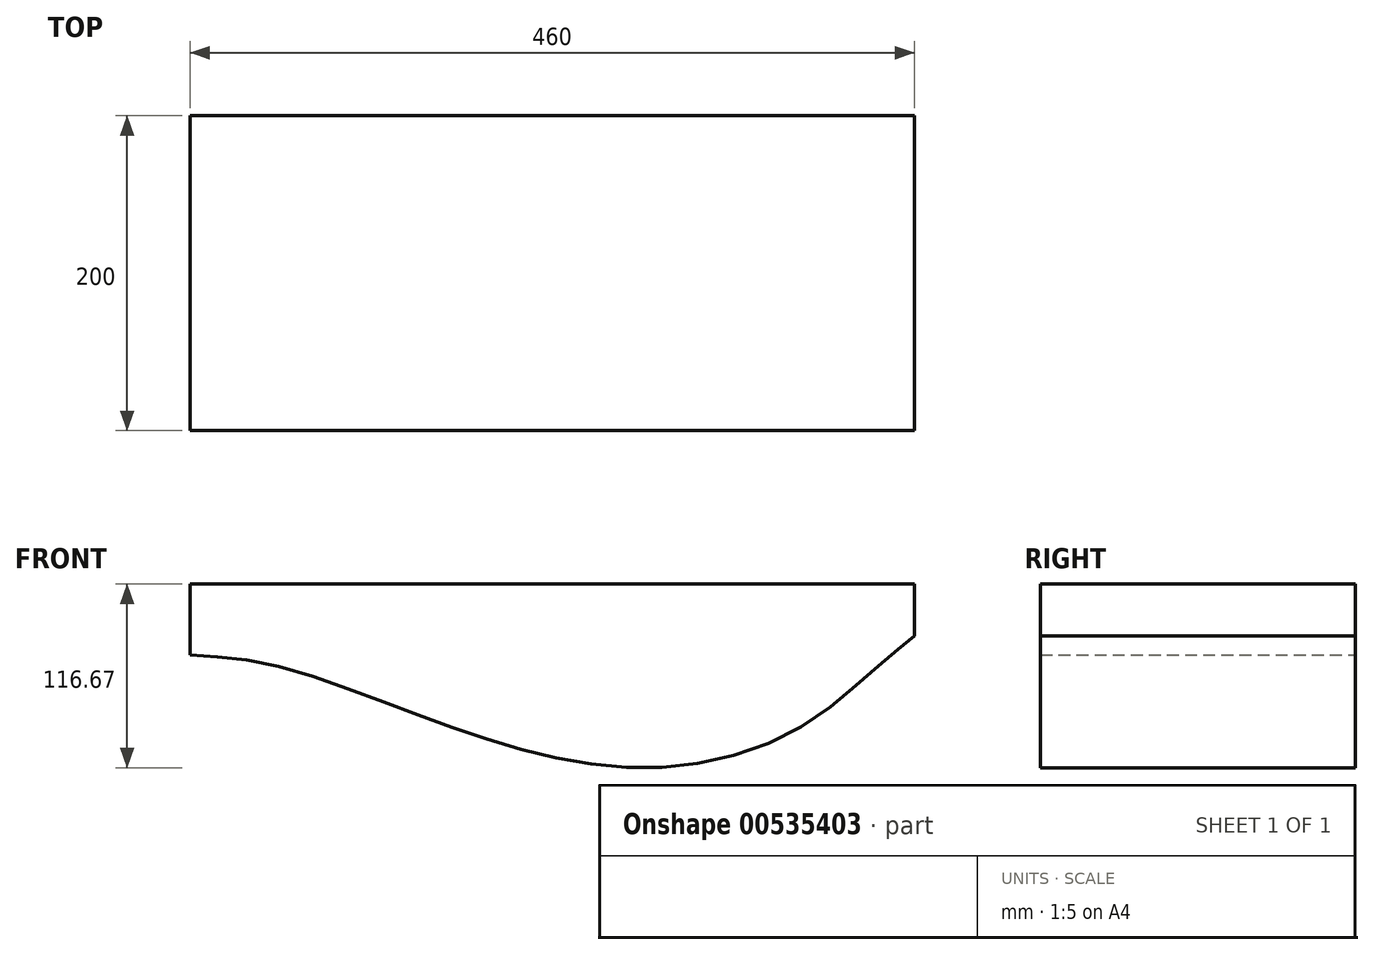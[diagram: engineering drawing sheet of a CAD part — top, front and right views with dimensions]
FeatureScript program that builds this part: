
annotation { "Feature Type Name" : "Feature", "Feature Type Description" : "" }
export const myFeature = defineFeature(function(context is Context, id is Id, definition is map)
    precondition{}
    {
        {
            var Q0;
            Q0=qCreatedBy(makeId("Front.planeOp"),FACE);
            var sketch = newSketch(context, id + "F0", { "sketchPlane" : qUnion([Q0])});
            skLineSegment(sketch, "E0", {"start": v(-101.41, 43.82) * mm, "end": v(358.59, 43.82) * mm});
            skLineSegment(sketch, "E1", {"start": v(-101.41, 43.82) * mm, "end": v(-101.41, -1.18) * mm});
            skLineSegment(sketch, "E2", {"start": v(-78.41, 43.82) * mm, "end": v(-78.41, -3.18) * mm, "construction": true});
            skLineSegment(sketch, "E3", {"start": v(-55.41, 43.82) * mm, "end": v(-55.41, -6.18) * mm, "construction": true});
            skLineSegment(sketch, "E4", {"start": v(-32.41, 43.82) * mm, "end": v(-32.41, -11.18) * mm, "construction": true});
            skLineSegment(sketch, "E5", {"start": v(-9.41, 43.82) * mm, "end": v(-9.41, -19.18) * mm, "construction": true});
            skLineSegment(sketch, "E6", {"start": v(13.59, 43.82) * mm, "end": v(13.59, -28.18) * mm, "construction": true});
            skLineSegment(sketch, "E7", {"start": v(36.59, 43.82) * mm, "end": v(36.59, -36.18) * mm, "construction": true});
            skLineSegment(sketch, "E8", {"start": v(59.59, 43.82) * mm, "end": v(59.59, -45.18) * mm, "construction": true});
            skLineSegment(sketch, "E9", {"start": v(82.59, 43.82) * mm, "end": v(82.59, -53.18) * mm, "construction": true});
            skLineSegment(sketch, "E10", {"start": v(105.59, 43.82) * mm, "end": v(105.59, -60.18) * mm, "construction": true});
            skLineSegment(sketch, "E11", {"start": v(128.59, 43.82) * mm, "end": v(128.59, -66.18) * mm, "construction": true});
            skLineSegment(sketch, "E12", {"start": v(151.59, 43.82) * mm, "end": v(151.59, -70.18) * mm, "construction": true});
            skLineSegment(sketch, "E13", {"start": v(174.59, 43.82) * mm, "end": v(174.59, -72.18) * mm, "construction": true});
            skLineSegment(sketch, "E14", {"start": v(197.59, 43.82) * mm, "end": v(197.59, -72.18) * mm, "construction": true});
            skLineSegment(sketch, "E15", {"start": v(220.59, 43.82) * mm, "end": v(220.59, -70.18) * mm, "construction": true});
            skLineSegment(sketch, "E16", {"start": v(243.59, 43.82) * mm, "end": v(243.59, -64.18) * mm, "construction": true});
            skLineSegment(sketch, "E17", {"start": v(266.59, 43.82) * mm, "end": v(266.59, -56.18) * mm, "construction": true});
            skLineSegment(sketch, "E18", {"start": v(289.59, 43.82) * mm, "end": v(289.59, -45.18) * mm, "construction": true});
            skLineSegment(sketch, "E19", {"start": v(312.59, 43.82) * mm, "end": v(312.59, -28.18) * mm, "construction": true});
            skLineSegment(sketch, "E20", {"start": v(335.59, 43.82) * mm, "end": v(335.59, -8.18) * mm, "construction": true});
            skLineSegment(sketch, "E21", {"start": v(358.59, 43.82) * mm, "end": v(358.59, 10.82) * mm});
            skFitSpline(sketch, "E22", {"points": [v(-101.41, -1.18) * mm, v(-55.41, -6.18) * mm, v(13.59, -28.18) * mm, v(82.59, -53.18) * mm, v(151.59, -70.18) * mm, v(220.59, -70.18) * mm, v(289.59, -45.18) * mm, v(335.59, -8.18) * mm, v(358.59, 10.82) * mm], "startDerivative": vector(383.1, -22.63) * mm, "endDerivative": vector(225.97, 177.9) * mm});
            skSolve(sketch);
        }
        {
            var Q0;
            Q0=makeQuery(id+"F0.imprint","IMPRINT",FACE,{"disambiguationData":[TD([[makeQuery(id+"F0.imprint","IMPRINT",EDGE,{"derivedFrom":sQuery(id+"F0.wireOp",EDGE,"E0")}),-1.0]])]});
            extrude(context, id + "F1", {"entities" : qUnion([Q0]), "depth" : 200 * mm, "offsetDistance" : 25 * mm});
        }
    });
